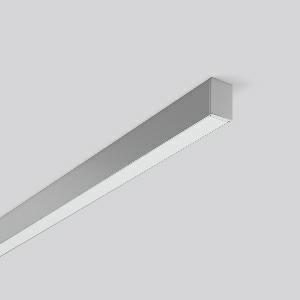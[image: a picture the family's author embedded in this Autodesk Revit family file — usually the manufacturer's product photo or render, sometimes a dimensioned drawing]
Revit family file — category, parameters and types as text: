
# Revit family: less_is_more_27_312196_0045_76_9db1
name_source: partatom
category: Lighting Fixtures
units: mm (PartAtom-declared; Revit-internal decimal feet)

## family parameters
Cut with Voids When Loaded = No
Host = Face
Light Source = No
Part Type = Normal
Room Calculation Point = No
Round Connector Dimension = Use Diameter
Shared = No

## types (1)
- LESS IS MORE 27 (1 x LED Modul 830, 1600 lm, 3000)
    Apparent Load = 29 VA
    CIE Flux Codes = 48 79 96 100 100
    Color Rendering = 80
    Color Temperature = 3000
    Default Elevation = 1800 mm
    Description = Series: LESS IS MORE 27
Ceiling and wall luminaire with slim design. Housing: extruded aluminium profile, powder-coated. End cap aluminium powder-coated. Diffuser made of non-yellowing plastic (PMMA), opal. Suitable for Ceiling mounting, Wall (surface). External driver with connecting cable. 
Colour: silver, matt (approx. RAL 9006)
Length: 1012 mm
Width: 28 mm
Height: 38 mm
Lamp: LED
Socket: without socket
Colour temperature: 3000K
Colour rendering index (CRI): 82
System power: 29 W
Rated luminous flux: 1600 lm
Luminous efficiency: 55 lm/W
Control gear: Voltage converter, DALI dim.
Protection class: II
Type of protection: IP 20
    Height = 38 mm
    Lamp = 1 x LED Modul 830
    Lamp Light Flux = 1600 lm
    Lamp count = 1
    Length = 1012 mm
    Lifetime = 50000 h
    Luminous efficacy = 55 lm/W
    Manufacturer = RZB
    ModVariant = No
    Model = 312196.0045.76
    Mounting Place = Wall, Ceiling
    Mounting Type = Surface mounted
    Number of Poles = 1
    OnlyDefault = Yes
    Power Factor = 1
    Product Name = LESS IS MORE 27
    Product group = Surface mounted LED linear luminaires
    ProductGroupID = 307
    Protection Class = Protection class II
    Protection Degree = IP 20
    RLX_Detail_Level = 1
    RLX_Emergency_Light_Flux = 0 lm
    RLX_Emergency_Type = 0
    RLX_Emergency_Type_DB = No
    RlxData = <blob elided: 25405 chars, md5=07cd4b3d>
    Socket = socket
    Standby Power = 0 W
    System Light Flux = 1600 lm
    System Power = 29 W
    Type Comments = Product without accessories
    Type Image = 312196.0045.jpg
    URL = http://relux.com
    VarID = ---
    Voltage = 230 V
    Voltage Range = 220-240 V
    Weight = 0.00 kg
    Width = 28 mm

## geometry (parser evidence)
native form markers: Blend x4, Sweep x11
no freeform markers — native parametric forms only
